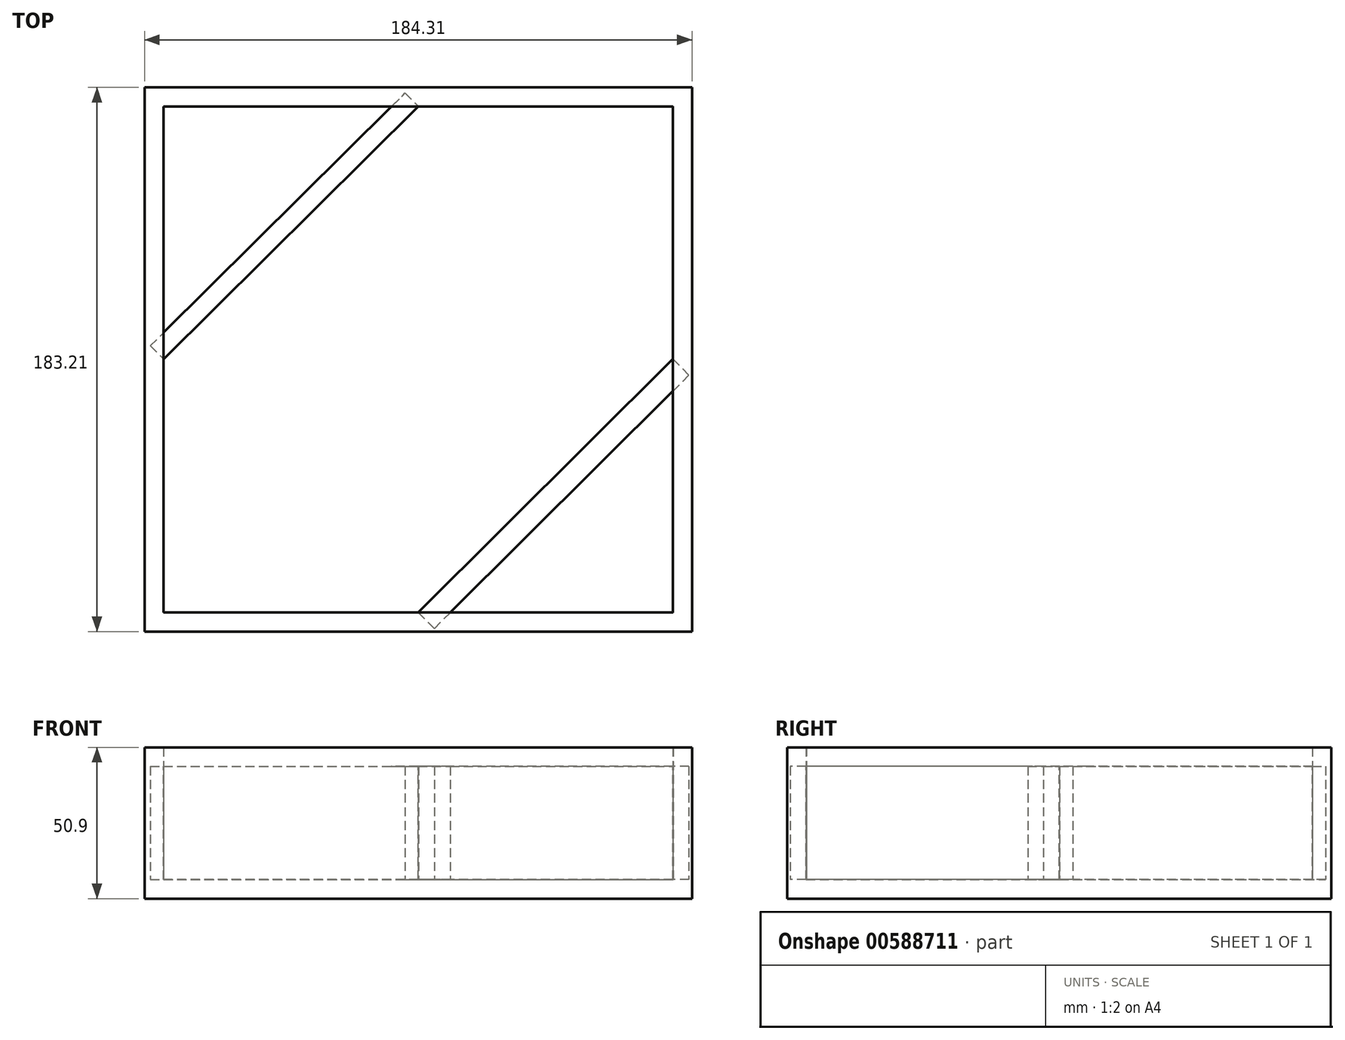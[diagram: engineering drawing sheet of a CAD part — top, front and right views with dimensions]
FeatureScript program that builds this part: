
annotation { "Feature Type Name" : "Feature", "Feature Type Description" : "" }
export const myFeature = defineFeature(function(context is Context, id is Id, definition is map)
    precondition{}
    {
        {
            var Q0;
            Q0=qCreatedBy(makeId("Top.planeOp"),FACE);
            var sketch = newSketch(context, id + "F0", { "sketchPlane" : qUnion([Q0])});
            skLineSegment(sketch, "E0.bottom", {"start": v(-91.93, 91.44) * mm, "end": v(92.28, 91.44) * mm});
            skLineSegment(sketch, "E0.top", {"start": v(-91.93, -91.67) * mm, "end": v(92.28, -91.67) * mm});
            skLineSegment(sketch, "E0.left", {"start": v(-91.93, 91.44) * mm, "end": v(-91.93, -91.67) * mm});
            skLineSegment(sketch, "E0.right", {"start": v(92.28, 91.44) * mm, "end": v(92.28, -91.67) * mm});
            skSolve(sketch);
        }
        {
            var Q0;
            Q0=makeQuery(id+"F0.imprint","IMPRINT",FACE,{"disambiguationData":[TD([[makeQuery(id+"F0.imprint","IMPRINT",EDGE,{"derivedFrom":sQuery(id+"F0.wireOp",EDGE,"E0.bottom")}),-1.0]])]});
            extrude(context, id + "F1", {"entities" : qUnion([Q0]), "endBound" : BoundingType.SYMMETRIC, "depth" : 50.8 * mm, "offsetDistance" : 25.4 * mm});
        }
        {
            var Q0;
            Q0=makeQuery(id+"F1.opExtrude","CAP_FACE",FACE,{"disambiguationData":[OSD([sQuery(id+"F0.wireOp",EDGE,"E0.bottom"),sQuery(id+"F0.wireOp",EDGE,"E0.top"),sQuery(id+"F0.wireOp",EDGE,"E0.left"),sQuery(id+"F0.wireOp",EDGE,"E0.right")])],"isStart":false});
            shell(context, id + "F2", {"entities" : qUnion([Q0]), "thickness" : 6.35 * mm});
        }
        {
            var Q0;
            Q0=makeQuery(id+"F2.opShell","OFFSET_FACE",FACE,{"disambiguationData":[OSD([sQuery(id+"F0.wireOp",EDGE,"E0.bottom"),sQuery(id+"F0.wireOp",EDGE,"E0.top"),sQuery(id+"F0.wireOp",EDGE,"E0.left"),sQuery(id+"F0.wireOp",EDGE,"E0.right")])]});
            var sketch = newSketch(context, id + "F3", { "sketchPlane" : qUnion([Q0])});
            skLineSegment(sketch, "E1", {"start": v(-85.58, 0) * mm, "end": v(0.17, 85.09) * mm});
            skLineSegment(sketch, "E2", {"start": v(0.17, 85.09) * mm, "end": v(84.6, 0) * mm});
            skSolve(sketch);
        }
        {
            var Q0;
            {var subQ0=sQuery(id+"F3.wireOp",EDGE,"E1");Q0=makeQuery(id+"F3.imprint","IMPRINT",FACE,{"disambiguationData":[TD([[makeQuery(id+"F3.imprint","IMPRINT",EDGE,{"derivedFrom":subQ0}),1.0]])]});}
            extrude(context, id + "F4", {"entities" : qUnion([Q0]), "operationType" : NewBodyOperationType.ADD, "depth" : 38.1 * mm, "offsetDistance" : 25.4 * mm});
        }
        {
            var Q0;
            Q0=makeQuery(id+"F4.opExtrude","CAP_FACE",FACE,{"disambiguationData":[OSD([sQuery(id+"F0.wireOp",EDGE,"E0.bottom"),sQuery(id+"F0.wireOp",EDGE,"E0.left"),sQuery(id+"F3.wireOp",EDGE,"E1")])],"isStart":false});
            var Q1;
            Q1=makeQuery(id+"F1.opExtrude","SWEPT_BODY",BODY,{"disambiguationData":[OSD([sQuery(id+"F0.wireOp",EDGE,"E0.bottom"),sQuery(id+"F0.wireOp",EDGE,"E0.top"),sQuery(id+"F0.wireOp",EDGE,"E0.left"),sQuery(id+"F0.wireOp",EDGE,"E0.right")])]});
            shell(context, id + "F5", {"entities" : qUnion([Q0]), "parts" : qUnion([Q1]), "thickness" : 0.03 * mm, "oppositeDirection" : true});
        }
        {
            var Q0;
            Q0=makeQuery(id+"F2.opShell","OFFSET_FACE",FACE,{"disambiguationData":[OSD([sQuery(id+"F0.wireOp",EDGE,"E0.bottom"),sQuery(id+"F0.wireOp",EDGE,"E0.top"),sQuery(id+"F0.wireOp",EDGE,"E0.left"),sQuery(id+"F0.wireOp",EDGE,"E0.right")])]});
            var sketch = newSketch(context, id + "F6", { "sketchPlane" : qUnion([Q0])});
            skLineSegment(sketch, "E3", {"start": v(85.9, 0) * mm, "end": v(0.17, -85.3) * mm});
            skPoint(sketch, "E3.startSnap0", {"position": v(85.9, -0.12) * mm});
            skSolve(sketch);
        }
        {
            var Q0;
            Q0 = qSketchRegion(id + "F6", true);
            var Q1;
            {var subQ0=sQuery(id+"F6.wireOp",EDGE,"E3");Q1=makeQuery(id+"F6.imprint","IMPRINT",FACE,{"disambiguationData":[TD([[makeQuery(id+"F6.imprint","IMPRINT",EDGE,{"derivedFrom":subQ0}),1.0]])]});}
            extrude(context, id + "F7", {"entities" : qUnion([Q0, Q1]), "operationType" : NewBodyOperationType.ADD, "depth" : 38.1 * mm, "offsetDistance" : 25.4 * mm});
        }
        {
            var Q0;
            Q0=makeQuery(id+"F7.opExtrude","CAP_FACE",FACE,{"disambiguationData":[OSD([sQuery(id+"F0.wireOp",EDGE,"E0.top"),sQuery(id+"F0.wireOp",EDGE,"E0.right"),sQuery(id+"F6.wireOp",EDGE,"E3")])],"isStart":false});
            shell(context, id + "F8", {"entities" : qUnion([Q0]), "thickness" : 0.03 * mm, "oppositeDirection" : true});
        }
        {
            var Q0;
            Q0=makeQuery(id+"F4.opExtrude","SWEPT_FACE",FACE,{"disambiguationData":[OSD([sQuery(id+"F3.wireOp",EDGE,"E1")])]});
            extrude(context, id + "F9", {"entities" : qUnion([Q0]), "operationType" : NewBodyOperationType.ADD, "depth" : -6.35 * mm, "offsetDistance" : 25.4 * mm});
        }
        {
            var Q0;
            Q0=makeQuery(id+"F7.opExtrude","SWEPT_FACE",FACE,{"disambiguationData":[OSD([sQuery(id+"F6.wireOp",EDGE,"E3")])]});
            extrude(context, id + "F10", {"entities" : qUnion([Q0]), "operationType" : NewBodyOperationType.ADD, "oppositeDirection" : true, "depth" : 7.64 * mm, "offsetDistance" : 25.4 * mm});
        }
    });
